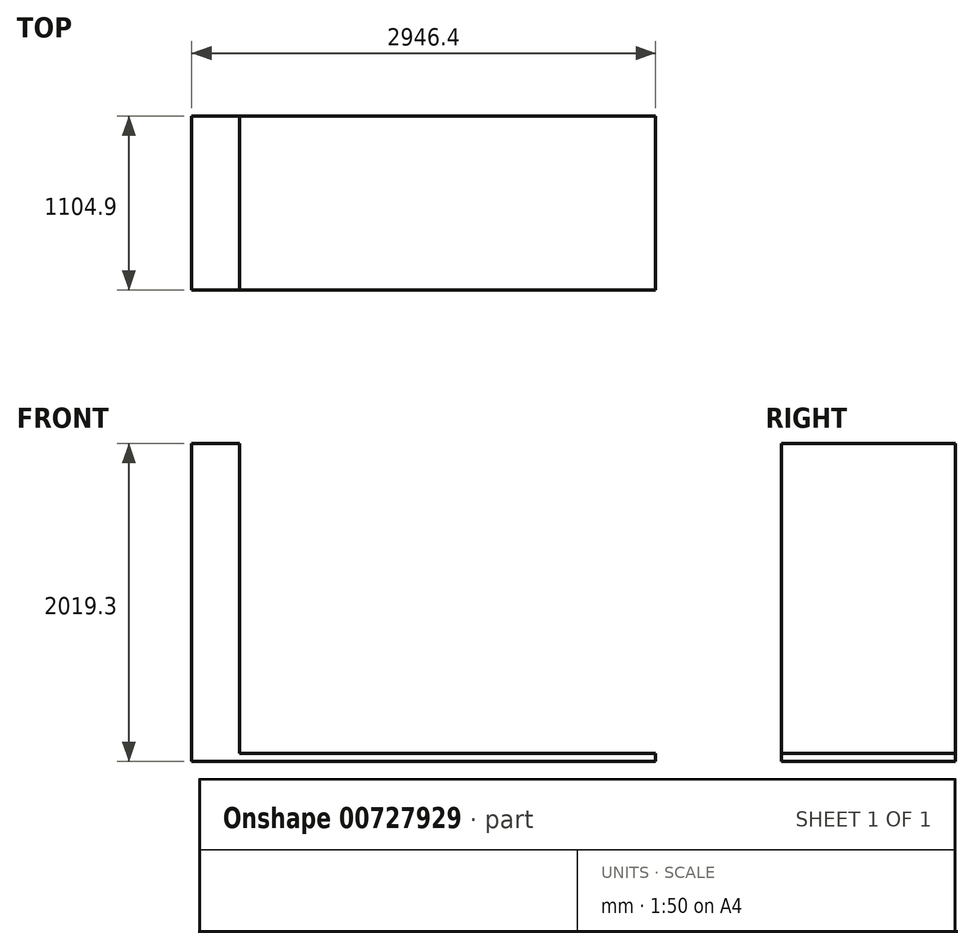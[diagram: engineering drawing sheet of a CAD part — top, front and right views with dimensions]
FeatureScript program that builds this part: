
annotation { "Feature Type Name" : "Feature", "Feature Type Description" : "" }
export const myFeature = defineFeature(function(context is Context, id is Id, definition is map)
    precondition{}
    {
        {
            var Q0;
            Q0=qCreatedBy(makeId("Front.planeOp"),FACE);
            var sketch = newSketch(context, id + "F0", { "sketchPlane" : qUnion([Q0])});
            skLineSegment(sketch, "E0.bottom", {"start": v(0, 0) * mm, "end": v(304.8, 0) * mm});
            skLineSegment(sketch, "E0.top", {"start": v(0, 2019.3) * mm, "end": v(304.8, 2019.3) * mm});
            skLineSegment(sketch, "E0.left", {"start": v(0, 0) * mm, "end": v(0, 2019.3) * mm});
            skLineSegment(sketch, "E0.right", {"start": v(304.8, 50.8) * mm, "end": v(304.8, 2019.3) * mm});
            skLineSegment(sketch, "E1.bottom", {"start": v(0, 0) * mm, "end": v(2946.4, 0) * mm});
            skLineSegment(sketch, "E1.top", {"start": v(304.8, 50.8) * mm, "end": v(2946.4, 50.8) * mm});
            skLineSegment(sketch, "E1.left", {"start": v(0, 0) * mm, "end": v(0, 50.8) * mm});
            skLineSegment(sketch, "E1.right", {"start": v(2946.4, 0) * mm, "end": v(2946.4, 50.8) * mm});
            skSolve(sketch);
        }
        {
            var Q0;
            Q0 = qSketchRegion(id + "F0", true);
            extrude(context, id + "F1", {"entities" : qUnion([Q0]), "depth" : 1104.9 * mm, "offsetDistance" : 25.4 * mm});
        }
        {
            var Q0;
            Q0=makeQuery(id+"F1.opExtrude","SWEPT_FACE",FACE,{"disambiguationData":[OSD([sQuery(id+"F0.wireOp",EDGE,"E0.right")])]});
            var sketch = newSketch(context, id + "F2", { "sketchPlane" : qUnion([Q0])});
            skLineSegment(sketch, "E2", {"start": v(-1104.9, 1715.16) * mm, "end": v(0, 1715.16) * mm, "construction": true});
            skPoint(sketch, "E3", {"position": v(-1073.15, 1715.16) * mm});
            skPoint(sketch, "E4", {"position": v(-742.95, 1715.16) * mm});
            skPoint(sketch, "E5", {"position": v(-361.95, 1715.16) * mm});
            skPoint(sketch, "E6", {"position": v(-31.75, 1715.16) * mm});
            skSolve(sketch);
        }
    });
